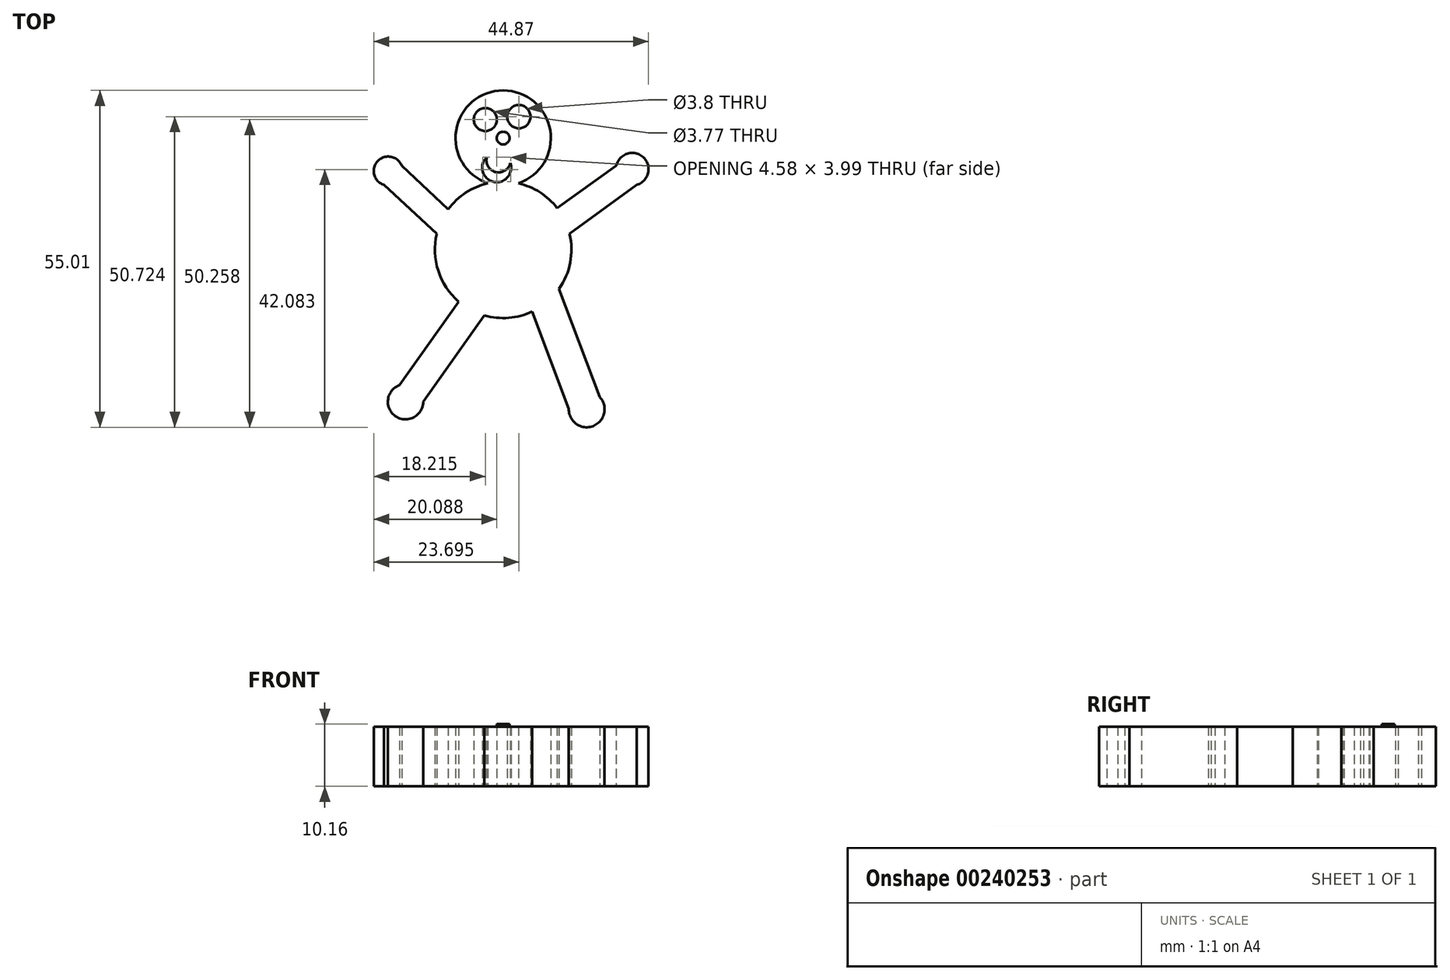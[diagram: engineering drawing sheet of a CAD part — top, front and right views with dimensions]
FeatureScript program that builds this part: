
annotation { "Feature Type Name" : "Feature", "Feature Type Description" : "" }
export const myFeature = defineFeature(function(context is Context, id is Id, definition is map)
    precondition{}
    {
        {
            var Q0;
            Q0=qCreatedBy(makeId("Top.planeOp"),FACE);
            var sketch = newSketch(context, id + "F0", { "sketchPlane" : qUnion([Q0])});
            skArc(sketch, "E0", {"start": v(6.2, 27.17) * mm, "mid": v(0, 65.08) * mm, "end": v(-6.2, 27.17) * mm});
            skArc(sketch, "E1", {"start": v(-6.2, 27.17) * mm, "mid": v(-15.25, 23.33) * mm, "end": v(-22.4, 16.58) * mm});
            skLineSegment(sketch, "E2", {"start": v(-22.4, 16.58) * mm, "end": v(-41.39, 34.25) * mm});
            skLineSegment(sketch, "E3", {"start": v(-48.59, 26.5) * mm, "end": v(-27.1, 6.51) * mm});
            skLineSegment(sketch, "E4", {"start": v(27.1, 6.51) * mm, "end": v(54.5, 26.5) * mm});
            skLineSegment(sketch, "E5", {"start": v(46.19, 34.25) * mm, "end": v(22.05, 17.05) * mm});
            skArc(sketch, "E6.trimOffspring", {"start": v(-27.1, 6.51) * mm, "mid": v(-26.51, -8.6) * mm, "end": v(-18.12, -21.17) * mm});
            skArc(sketch, "E7.trimOffspring", {"start": v(22.05, 17.05) * mm, "mid": v(15, 23.49) * mm, "end": v(6.2, 27.17) * mm});
            skLineSegment(sketch, "E8", {"start": v(-18.12, -21.17) * mm, "end": v(-42.26, -55.23) * mm});
            skLineSegment(sketch, "E9", {"start": v(-32.64, -62.05) * mm, "end": v(-7.65, -26.8) * mm});
            skLineSegment(sketch, "E10", {"start": v(11.89, -25.2) * mm, "end": v(26.82, -64.85) * mm});
            skLineSegment(sketch, "E11", {"start": v(39.4, -60.12) * mm, "end": v(22.8, -16.03) * mm});
            skArc(sketch, "E12.trimOffspring", {"start": v(-7.65, -26.8) * mm, "mid": v(2.26, -27.78) * mm, "end": v(11.89, -25.2) * mm});
            skArc(sketch, "E13.trimOffspring", {"start": v(22.8, -16.03) * mm, "mid": v(27.38, -5.22) * mm, "end": v(27.1, 6.51) * mm});
            skArc(sketch, "E14", {"start": v(54.5, 26.5) * mm, "mid": v(57.24, 37.79) * mm, "end": v(46.19, 34.25) * mm});
            skArc(sketch, "E15", {"start": v(-41.39, 34.25) * mm, "mid": v(-51.25, 36.2) * mm, "end": v(-48.59, 26.5) * mm});
            skArc(sketch, "E16", {"start": v(-42.26, -55.23) * mm, "mid": v(-44.02, -67.9) * mm, "end": v(-32.64, -62.05) * mm});
            skArc(sketch, "E17", {"start": v(26.82, -64.85) * mm, "mid": v(36.68, -71.99) * mm, "end": v(39.4, -60.12) * mm});
            skSolve(sketch);
        }
        {
            var Q0;
            Q0 = qSketchRegion(id + "F0", true);
            extrude(context, id + "F1", {"entities" : qUnion([Q0]), "depth" : 24.38 * mm});
        }
        {
            var Q0;
            Q0=qCreatedBy(makeId("Top.planeOp"),FACE);
            var sketch = newSketch(context, id + "F2", { "sketchPlane" : qUnion([Q0])});
            skCircle(sketch, "E18", {"center": v(-7.29, 53.2) * mm, "radius": 4.7 * mm});
            skCircle(sketch, "E19", {"center": v(6.41, 54.36) * mm, "radius": 4.74 * mm});
            skSolve(sketch);
        }
        {
            var Q0;
            Q0 = qSketchRegion(id + "F2", true);
            extrude(context, id + "F3", {"entities" : qUnion([Q0]), "operationType" : NewBodyOperationType.REMOVE, "depth" : 51.56 * mm});
        }
        {
            var Q0;
            Q0=qCreatedBy(makeId("Top.planeOp"),FACE);
            var sketch = newSketch(context, id + "F4", { "sketchPlane" : qUnion([Q0])});
            skCircle(sketch, "E20", {"center": v(0, 45.62) * mm, "radius": 2.6 * mm});
            skSolve(sketch);
        }
        {
            var Q0;
            Q0 = qSketchRegion(id + "F4", true);
            extrude(context, id + "F5", {"entities" : qUnion([Q0]), "operationType" : NewBodyOperationType.ADD, "depth" : 25.4 * mm});
        }
        {
            var Q0;
            Q0=qCreatedBy(makeId("Top.planeOp"),FACE);
            var sketch = newSketch(context, id + "F6", { "sketchPlane" : qUnion([Q0])});
            skArc(sketch, "E21", {"start": v(-6.7, 37.75) * mm, "mid": v(-3.06, 31.76) * mm, "end": v(2.91, 35.41) * mm});
            skArc(sketch, "E22", {"start": v(-6.7, 37.75) * mm, "mid": v(-4.03, 27.77) * mm, "end": v(2.91, 35.41) * mm});
            skSolve(sketch);
        }
        {
            var Q0;
            Q0 = qSketchRegion(id + "F6", true);
            extrude(context, id + "F7", {"entities" : qUnion([Q0]), "operationType" : NewBodyOperationType.REMOVE, "depth" : 54.36 * mm});
        }
        {
            var Q0;
            Q0=makeQuery(id+"F1.opExtrude","SWEPT_BODY",BODY,{"disambiguationData":[OSD([sQuery(id+"F0.wireOp",EDGE,"E0"),sQuery(id+"F0.wireOp",EDGE,"E1"),sQuery(id+"F0.wireOp",EDGE,"E2"),sQuery(id+"F0.wireOp",EDGE,"E3"),sQuery(id+"F0.wireOp",EDGE,"E4"),sQuery(id+"F0.wireOp",EDGE,"E5"),sQuery(id+"F0.wireOp",EDGE,"E6.trimOffspring"),sQuery(id+"F0.wireOp",EDGE,"E7.trimOffspring"),sQuery(id+"F0.wireOp",EDGE,"E8"),sQuery(id+"F0.wireOp",EDGE,"E9"),sQuery(id+"F0.wireOp",EDGE,"E10"),sQuery(id+"F0.wireOp",EDGE,"E11"),sQuery(id+"F0.wireOp",EDGE,"E12.trimOffspring"),sQuery(id+"F0.wireOp",EDGE,"E13.trimOffspring"),sQuery(id+"F0.wireOp",EDGE,"E14"),sQuery(id+"F0.wireOp",EDGE,"E15"),sQuery(id+"F0.wireOp",EDGE,"E16"),sQuery(id+"F0.wireOp",EDGE,"E17")])]});
            var Q1;
            Q1=qCreatedBy(makeId("Origin.pointOp"),VERTEX);
            transform(context, id + "F8", {"entities" : qUnion([Q0]), "transformType" : TransformType.SCALE_UNIFORMLY, "scale" : .2, "scalePoint" : qUnion([Q1]), "makeCopy" : false});
        }
        {
            var Q0;
            Q0=makeQuery(id+"F1.opExtrude","SWEPT_BODY",BODY,{"disambiguationData":[OSD([sQuery(id+"F0.wireOp",EDGE,"E0"),sQuery(id+"F0.wireOp",EDGE,"E1"),sQuery(id+"F0.wireOp",EDGE,"E2"),sQuery(id+"F0.wireOp",EDGE,"E3"),sQuery(id+"F0.wireOp",EDGE,"E4"),sQuery(id+"F0.wireOp",EDGE,"E5"),sQuery(id+"F0.wireOp",EDGE,"E6.trimOffspring"),sQuery(id+"F0.wireOp",EDGE,"E7.trimOffspring"),sQuery(id+"F0.wireOp",EDGE,"E8"),sQuery(id+"F0.wireOp",EDGE,"E9"),sQuery(id+"F0.wireOp",EDGE,"E10"),sQuery(id+"F0.wireOp",EDGE,"E11"),sQuery(id+"F0.wireOp",EDGE,"E12.trimOffspring"),sQuery(id+"F0.wireOp",EDGE,"E13.trimOffspring"),sQuery(id+"F0.wireOp",EDGE,"E14"),sQuery(id+"F0.wireOp",EDGE,"E15"),sQuery(id+"F0.wireOp",EDGE,"E16"),sQuery(id+"F0.wireOp",EDGE,"E17")])]});
            var Q1;
            Q1=qCreatedBy(makeId("Origin.pointOp"),VERTEX);
            transform(context, id + "F9", {"entities" : qUnion([Q0]), "transformType" : TransformType.SCALE_UNIFORMLY, "scale" : 2, "scalePoint" : qUnion([Q1]), "makeCopy" : false});
        }
    });
